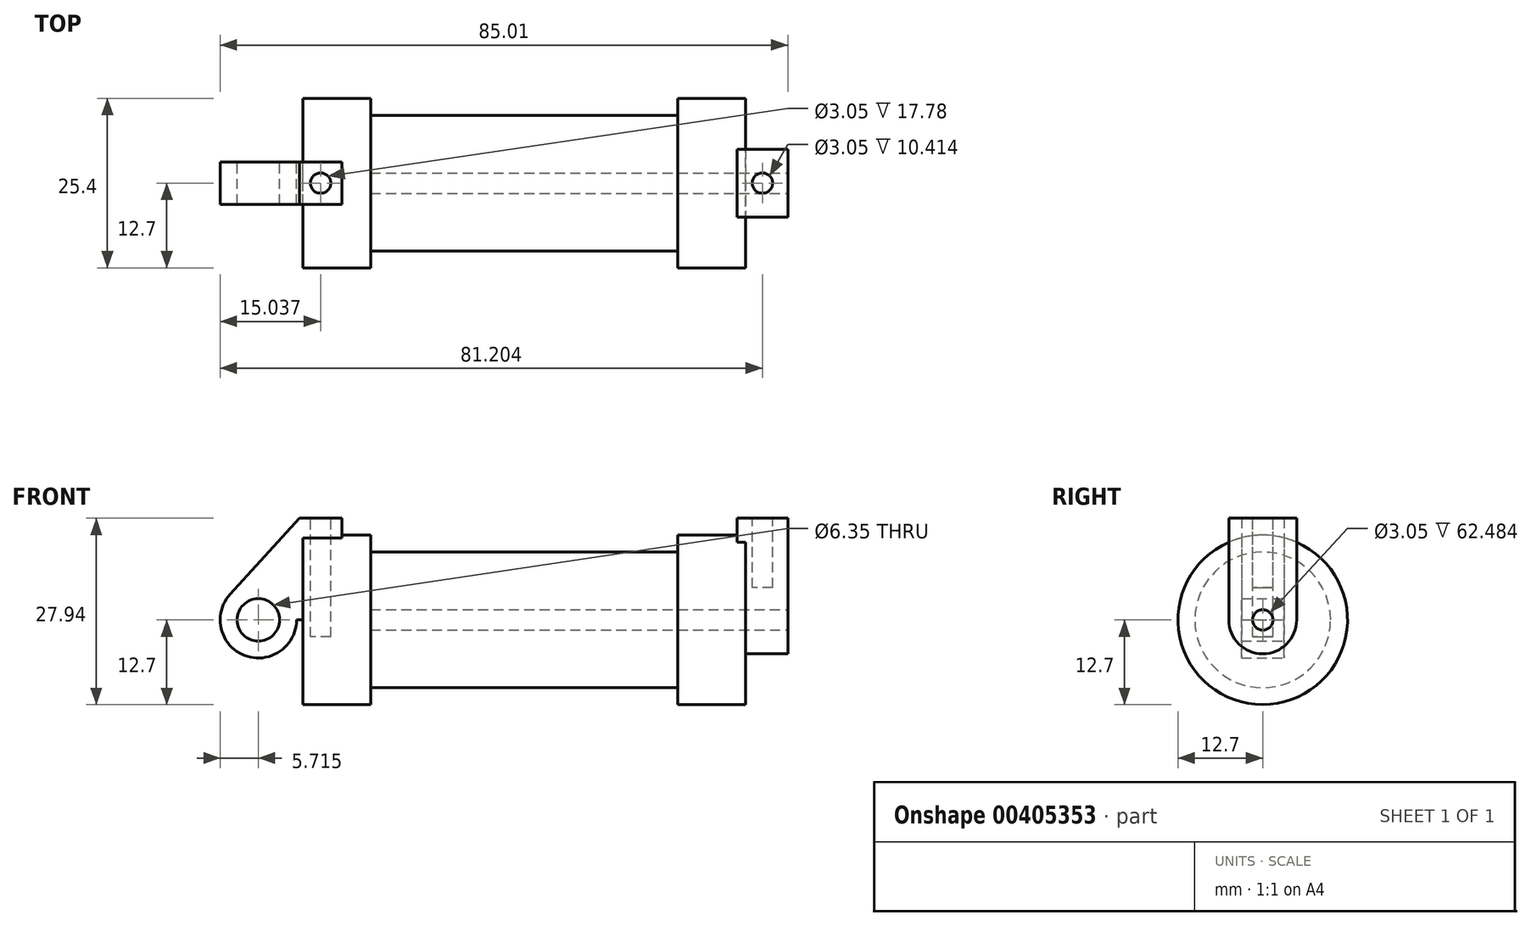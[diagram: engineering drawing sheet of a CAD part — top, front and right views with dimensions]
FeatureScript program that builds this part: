
annotation { "Feature Type Name" : "Feature", "Feature Type Description" : "" }
export const myFeature = defineFeature(function(context is Context, id is Id, definition is map)
    precondition{}
    {
        {
            var Q0;
            Q0=qCreatedBy(makeId("Front.planeOp"),FACE);
            var sketch = newSketch(context, id + "F0", { "sketchPlane" : qUnion([Q0])});
            skLineSegment(sketch, "E0", {"start": v(0, 0) * mm, "end": v(0, 12.7) * mm});
            skLineSegment(sketch, "E1", {"start": v(0, 12.7) * mm, "end": v(10.16, 12.7) * mm});
            skLineSegment(sketch, "E2", {"start": v(10.16, 12.7) * mm, "end": v(10.16, 10.16) * mm});
            skLineSegment(sketch, "E3", {"start": v(10.16, 10.16) * mm, "end": v(56.13, 10.16) * mm});
            skLineSegment(sketch, "E4", {"start": v(56.13, 10.16) * mm, "end": v(56.13, 12.7) * mm});
            skLineSegment(sketch, "E5", {"start": v(56.13, 12.7) * mm, "end": v(66.3, 12.7) * mm});
            skLineSegment(sketch, "E6", {"start": v(66.3, 12.7) * mm, "end": v(66.3, 0) * mm});
            skLineSegment(sketch, "E7", {"start": v(66.3, 0) * mm, "end": v(0, 0) * mm});
            skLineSegment(sketch, "E8", {"start": v(5.84, 15.24) * mm, "end": v(-0.5, 15.24) * mm});
            skLineSegment(sketch, "E9", {"start": v(-0.5, 15.24) * mm, "end": v(-10.88, 3.85) * mm});
            skLineSegment(sketch, "E10", {"start": v(0, 0) * mm, "end": v(-6.65, 0) * mm});
            skCircle(sketch, "E11", {"center": v(-6.65, 0) * mm, "radius": 5.72 * mm});
            skCircle(sketch, "E12", {"center": v(-6.65, 0) * mm, "radius": 3.18 * mm});
            skLineSegment(sketch, "E13", {"start": v(5.84, 15.24) * mm, "end": v(5.84, -9.4) * mm});
            skLineSegment(sketch, "E14", {"start": v(5.84, -9.4) * mm, "end": v(-8.18, -5.5) * mm});
            skSolve(sketch);
        }
        {
            var Q0;
            {var subQ0=sQuery(id+"F0.wireOp",EDGE,"E2");Q0=makeQuery(id+"F0.imprint","IMPRINT",FACE,{"disambiguationData":[TD([[makeQuery(id+"F0.imprint","IMPRINT",EDGE,{"derivedFrom":subQ0}),-1.0]])]});}
            var Q1;
            {var subQ0=sQuery(id+"F0.wireOp",EDGE,"E0");Q1=makeQuery(id+"F0.imprint","IMPRINT",FACE,{"disambiguationData":[TD([[makeQuery(id+"F0.imprint","IMPRINT",EDGE,{"derivedFrom":subQ0}),-1.0]])]});}
            var Q2;
            Q2=sQuery(id+"F0.wireOp",EDGE,"E7");
            revolve(context, id + "F1", {"entities" : qUnion([Q0, Q1]), "axis" : qUnion([Q2]), "revolveType" : RevolveType.FULL});
        }
        {
            var Q0;
            {var subQ1=sQuery(id+"F0.wireOp",EDGE,"E0");Q0=makeQuery(id+"F0.imprint","IMPRINT",FACE,{"disambiguationData":[TD([[makeQuery(id+"F0.imprint","IMPRINT",EDGE,{"derivedFrom":subQ1}),1.0]])]});}
            var Q1;
            {var subQ5=sQuery(id+"F0.wireOp",EDGE,"E12");Q1=makeQuery(id+"F0.imprint","IMPRINT",FACE,{"disambiguationData":[TD([[makeQuery(id+"F0.imprint","IMPRINT",EDGE,{"derivedFrom":subQ5}),-1.0]])]});}
            var Q2;
            {var subQ0=sQuery(id+"F0.wireOp",EDGE,"E0");Q2=makeQuery(id+"F0.imprint","IMPRINT",FACE,{"disambiguationData":[TD([[makeQuery(id+"F0.imprint","IMPRINT",EDGE,{"derivedFrom":subQ0}),-1.0]])]});}
            extrude(context, id + "F2", {"entities" : qUnion([Q0, Q1, Q2]), "operationType" : NewBodyOperationType.ADD, "endBound" : BoundingType.SYMMETRIC, "depth" : 6.35 * mm});
        }
        {
            var Q0;
            Q0=makeQuery(id+"F1.opRevolve","SWEPT_FACE",FACE,{"disambiguationData":[OSD([sQuery(id+"F0.wireOp",EDGE,"E6")])]});
            var sketch = newSketch(context, id + "F3", { "sketchPlane" : qUnion([Q0])});
            skCircle(sketch, "E15", {"center": v(0, 0) * mm, "radius": 1.52 * mm});
            skCircle(sketch, "E16", {"center": v(0, 0) * mm, "radius": 5.08 * mm});
            skLineSegment(sketch, "E17", {"start": v(-5.08, 0) * mm, "end": v(-5.08, 15.24) * mm});
            skLineSegment(sketch, "E18.MirrorCS", {"start": v(5.08, 0) * mm, "end": v(5.08, 15.24) * mm});
            skLineSegment(sketch, "E19", {"start": v(-5.08, 15.24) * mm, "end": v(5.08, 15.24) * mm});
            skSolve(sketch);
        }
        {
            var Q0;
            Q0=qSketchRegion(id+"F3",true);
            extrude(context, id + "F4", {"entities" : qUnion([Q0]), "operationType" : NewBodyOperationType.ADD, "oppositeDirection" : true, "depth" : 1.27 * mm, "hasSecondDirection" : true, "secondDirectionOppositeDirection" : false, "secondDirectionDepth" : 6.35 * mm});
        }
        {
            var Q0;
            Q0=makeQuery(id+"F3.imprint","IMPRINT",FACE,{"disambiguationData":[TD([[makeQuery(id+"F3.imprint","IMPRINT",EDGE,{"derivedFrom":sQuery(id+"F3.wireOp",EDGE,"E15")}),1.0]])]});
            var Q1;
            Q1=sQuery(id+"F3.wireOp",EDGE,"E15");
            var Q2;
            Q2=makeQuery(id+"F1.opRevolve","SWEPT_FACE",FACE,{"disambiguationData":[OSD([sQuery(id+"F0.wireOp",EDGE,"E2")])]});
            extrude(context, id + "F5", {"entities" : qUnion([Q0]), "operationType" : NewBodyOperationType.REMOVE, "surfaceEntities" : qUnion([Q1]), "endBound" : BoundingType.UP_TO_SURFACE, "oppositeDirection" : true, "endBoundEntityFace" : qUnion([Q2]), "depth" : 33.86 * mm});
        }
        {
            var Q0;
            {var subQ0=sQuery(id+"F3.wireOp",EDGE,"E19");Q0=makeQuery(id+"FvTNI2ZgH7zS7n4_1.boolean.opBoolean","MERGE",FACE,{"derivedFrom":[makeQuery(id+"F4.opExtrude","SWEPT_FACE",FACE,{"disambiguationData":[OSD([subQ0])]}),makeQuery(id+"FvTNI2ZgH7zS7n4_1.opExtrude","SWEPT_FACE",FACE,{"disambiguationData":[OSD([subQ0])]})]});}
            var sketch = newSketch(context, id + "F6", { "sketchPlane" : qUnion([Q0])});
            skCircle(sketch, "E20", {"center": v(68.83, 0) * mm, "radius": 1.52 * mm});
            skCircle(sketch, "E21", {"center": v(2.67, 0) * mm, "radius": 1.52 * mm});
            skSolve(sketch);
        }
        {
            var Q0;
            Q0=makeQuery(id+"F6.imprint","IMPRINT",FACE,{"disambiguationData":[TD([[makeQuery(id+"F6.imprint","IMPRINT",EDGE,{"derivedFrom":sQuery(id+"F6.wireOp",EDGE,"E21")}),1.0]])]});
            extrude(context, id + "F7", {"entities" : qUnion([Q0]), "operationType" : NewBodyOperationType.REMOVE, "oppositeDirection" : true, "depth" : 17.78 * mm});
        }
        {
            var Q0;
            Q0=makeQuery(id+"F6.imprint","IMPRINT",FACE,{"disambiguationData":[TD([[makeQuery(id+"F6.imprint","IMPRINT",EDGE,{"derivedFrom":sQuery(id+"F6.wireOp",EDGE,"E20")}),1.0]])]});
            extrude(context, id + "F8", {"entities" : qUnion([Q0]), "operationType" : NewBodyOperationType.REMOVE, "oppositeDirection" : true, "depth" : 10.4 * mm});
        }
    });
